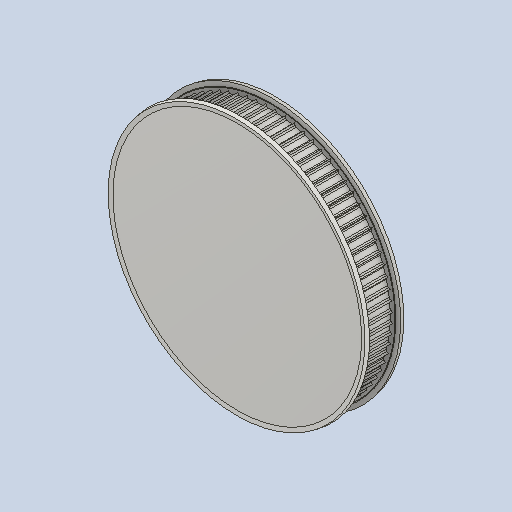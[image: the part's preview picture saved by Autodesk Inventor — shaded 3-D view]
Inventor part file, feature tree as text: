
AUTODESK INVENTOR PART (.ipt)
format: ipt  version: 2024 (Build 280153000, 153)  size: 574,464 bytes
history: native  units: mm (DEFAULTED — no unit token found)
features: other x3, extrude x2, fillet x1, pattern_circular x1
ambient origin geometry x8: Origin, YZ Plane, XZ Plane, XY Plane, X Axis, Y Axis, Z Axis, Center Point
bodies: Solid1 (feature_tree)
feature tree (7):
  other  "Pulley Sketch"
  extrude  "Base Body"  Depth=63.661977mm
  extrude  "Tooth"  Depth=0.3mm
  fillet  "Tooth Fillet"  Radius=1.25mm
  pattern_circular  "Teeth"  [2 undecoded]
  other  "Left flange"
  other  "Right flange"
note: 2 required parameter values undecoded (feature->parameter linkage not recoverable at this tier; creation-order binding heuristic only, values carry confidence <= 0.55)
